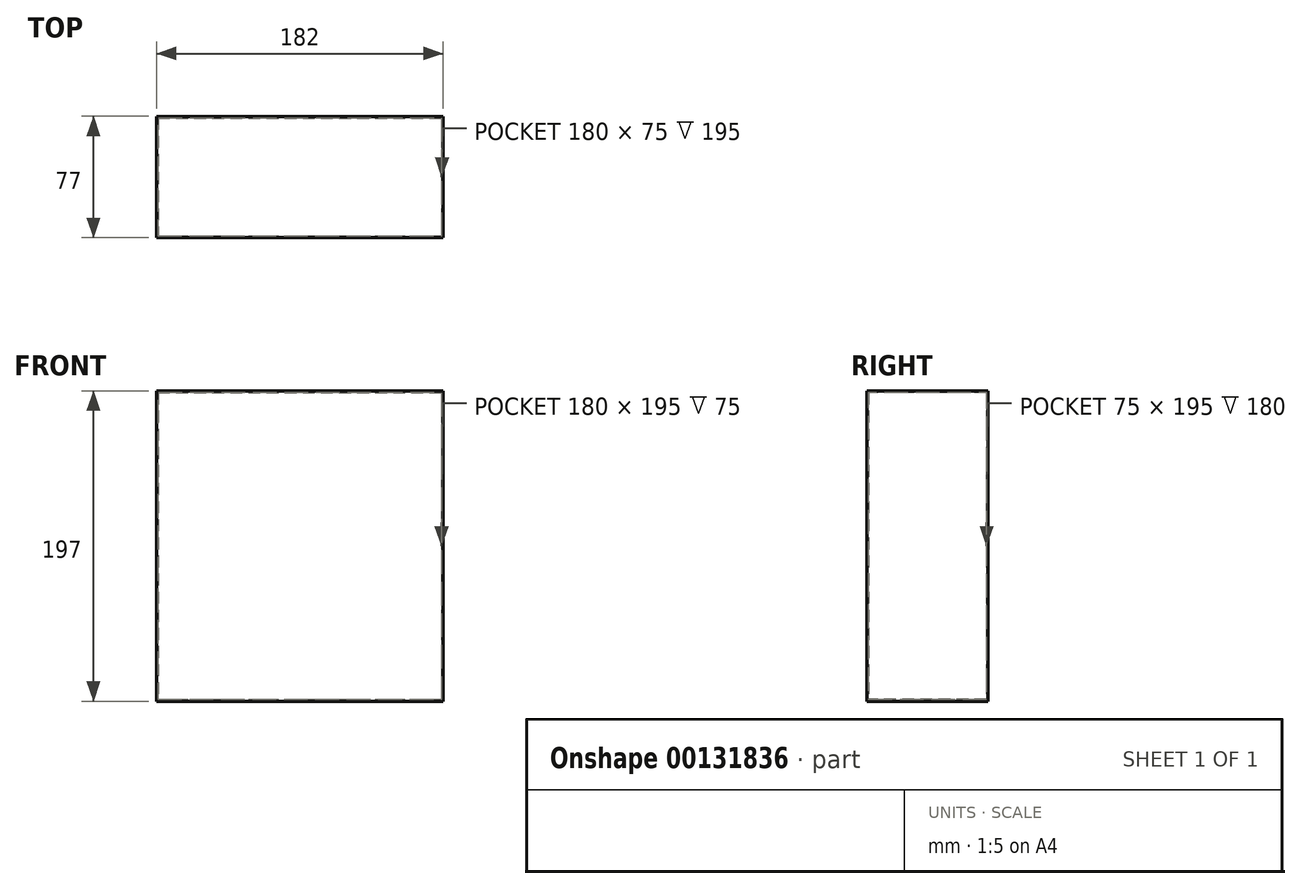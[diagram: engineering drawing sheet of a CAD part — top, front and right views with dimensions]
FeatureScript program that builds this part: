
annotation { "Feature Type Name" : "Feature", "Feature Type Description" : "" }
export const myFeature = defineFeature(function(context is Context, id is Id, definition is map)
    precondition{}
    {
        {
            var Q0;
            Q0=qCreatedBy(makeId("Top.planeOp"),FACE);
            var sketch = newSketch(context, id + "F0", { "sketchPlane" : qUnion([Q0])});
            skLineSegment(sketch, "E0.bottom", {"start": v(-150, 42.75) * mm, "end": v(30, 42.75) * mm});
            skLineSegment(sketch, "E0.top", {"start": v(-150, -32.25) * mm, "end": v(30, -32.25) * mm});
            skLineSegment(sketch, "E0.left", {"start": v(-150, 42.75) * mm, "end": v(-150, -32.25) * mm});
            skLineSegment(sketch, "E0.right", {"start": v(30, 42.75) * mm, "end": v(30, -32.25) * mm});
            skLineSegment(sketch, "E1.bottom", {"start": v(-151, 43.75) * mm, "end": v(31, 43.75) * mm});
            skLineSegment(sketch, "E1.top", {"start": v(-151, -33.25) * mm, "end": v(31, -33.25) * mm});
            skLineSegment(sketch, "E1.left", {"start": v(-151, 43.75) * mm, "end": v(-151, -33.25) * mm});
            skLineSegment(sketch, "E1.right", {"start": v(31, 43.75) * mm, "end": v(31, -33.25) * mm});
            skSolve(sketch);
        }
        {
            var Q0;
            Q0=makeQuery(id+"F0.imprint","IMPRINT",FACE,{"disambiguationData":[TD([[makeQuery(id+"F0.imprint","IMPRINT",EDGE,{"derivedFrom":sQuery(id+"F0.wireOp",EDGE,"E0.bottom")}),1.0]])]});
            extrude(context, id + "F1", {"entities" : qUnion([Q0]), "depth" : 195 * mm});
        }
        {
            var Q0;
            Q0=makeQuery(id+"F1.opExtrude","CAP_FACE",FACE,{"disambiguationData":[OSD([sQuery(id+"F0.wireOp",EDGE,"E0.bottom"),sQuery(id+"F0.wireOp",EDGE,"E0.top"),sQuery(id+"F0.wireOp",EDGE,"E0.left"),sQuery(id+"F0.wireOp",EDGE,"E0.right"),sQuery(id+"F0.wireOp",EDGE,"E1.bottom"),sQuery(id+"F0.wireOp",EDGE,"E1.top"),sQuery(id+"F0.wireOp",EDGE,"E1.left"),sQuery(id+"F0.wireOp",EDGE,"E1.right")])],"isStart":false});
            var sketch = newSketch(context, id + "F2", { "sketchPlane" : qUnion([Q0])});
            skLineSegment(sketch, "E2.bottom", {"start": v(-151, 43.75) * mm, "end": v(31, 43.75) * mm});
            skLineSegment(sketch, "E2.top", {"start": v(-151, -33.25) * mm, "end": v(31, -33.25) * mm});
            skLineSegment(sketch, "E2.left", {"start": v(-151, 43.75) * mm, "end": v(-151, -33.25) * mm});
            skLineSegment(sketch, "E2.right", {"start": v(31, 43.75) * mm, "end": v(31, -33.25) * mm});
            skSolve(sketch);
        }
        {
            var Q0;
            Q0=makeQuery(id+"F2.imprint","IMPRINT",FACE,{"disambiguationData":[TD([[makeQuery(id+"F2.imprint","IMPRINT",EDGE,{"derivedFrom":sQuery(id+"F2.wireOp",EDGE,"E2.bottom")}),-1.0]])]});
            var Q1;
            Q1=makeQuery(id+"F2.imprint","IMPRINT",FACE,{"disambiguationData":[TD([[makeQuery(id+"F2.imprint","IMPRINT",EDGE,{"derivedFrom":makeQuery(id+"F1.opExtrude","CAP_EDGE",EDGE,{"disambiguationData":[OSD([sQuery(id+"F0.wireOp",EDGE,"E0.bottom")])],"isStart":false})}),-1.0]])]});
            extrude(context, id + "F3", {"entities" : qUnion([Q0, Q1]), "operationType" : NewBodyOperationType.ADD, "depth" : 1 * mm});
        }
        {
            var Q0;
            Q0=makeQuery(id+"F1.opExtrude","CAP_FACE",FACE,{"disambiguationData":[OSD([sQuery(id+"F0.wireOp",EDGE,"E0.bottom"),sQuery(id+"F0.wireOp",EDGE,"E0.top"),sQuery(id+"F0.wireOp",EDGE,"E0.left"),sQuery(id+"F0.wireOp",EDGE,"E0.right"),sQuery(id+"F0.wireOp",EDGE,"E1.bottom"),sQuery(id+"F0.wireOp",EDGE,"E1.top"),sQuery(id+"F0.wireOp",EDGE,"E1.left"),sQuery(id+"F0.wireOp",EDGE,"E1.right")])],"isStart":true});
            var sketch = newSketch(context, id + "F4", { "sketchPlane" : qUnion([Q0])});
            skLineSegment(sketch, "E3.bottom", {"start": v(-151, 33.25) * mm, "end": v(31, 33.25) * mm});
            skLineSegment(sketch, "E3.top", {"start": v(-151, -43.75) * mm, "end": v(31, -43.75) * mm});
            skLineSegment(sketch, "E3.left", {"start": v(-151, 33.25) * mm, "end": v(-151, -43.75) * mm});
            skLineSegment(sketch, "E3.right", {"start": v(31, 33.25) * mm, "end": v(31, -43.75) * mm});
            skSolve(sketch);
        }
        {
            var Q0;
            Q0=makeQuery(id+"F4.imprint","IMPRINT",FACE,{"disambiguationData":[TD([[makeQuery(id+"F4.imprint","IMPRINT",EDGE,{"derivedFrom":sQuery(id+"F4.wireOp",EDGE,"E3.bottom")}),-1.0]])]});
            var Q1;
            Q1=makeQuery(id+"F4.imprint","IMPRINT",FACE,{"disambiguationData":[TD([[makeQuery(id+"F4.imprint","IMPRINT",EDGE,{"derivedFrom":makeQuery(id+"F1.opExtrude","CAP_EDGE",EDGE,{"disambiguationData":[OSD([sQuery(id+"F0.wireOp",EDGE,"E0.bottom")])],"isStart":true})}),1.0]])]});
            extrude(context, id + "F5", {"entities" : qUnion([Q0, Q1]), "operationType" : NewBodyOperationType.ADD, "depth" : 1 * mm});
        }
    });
